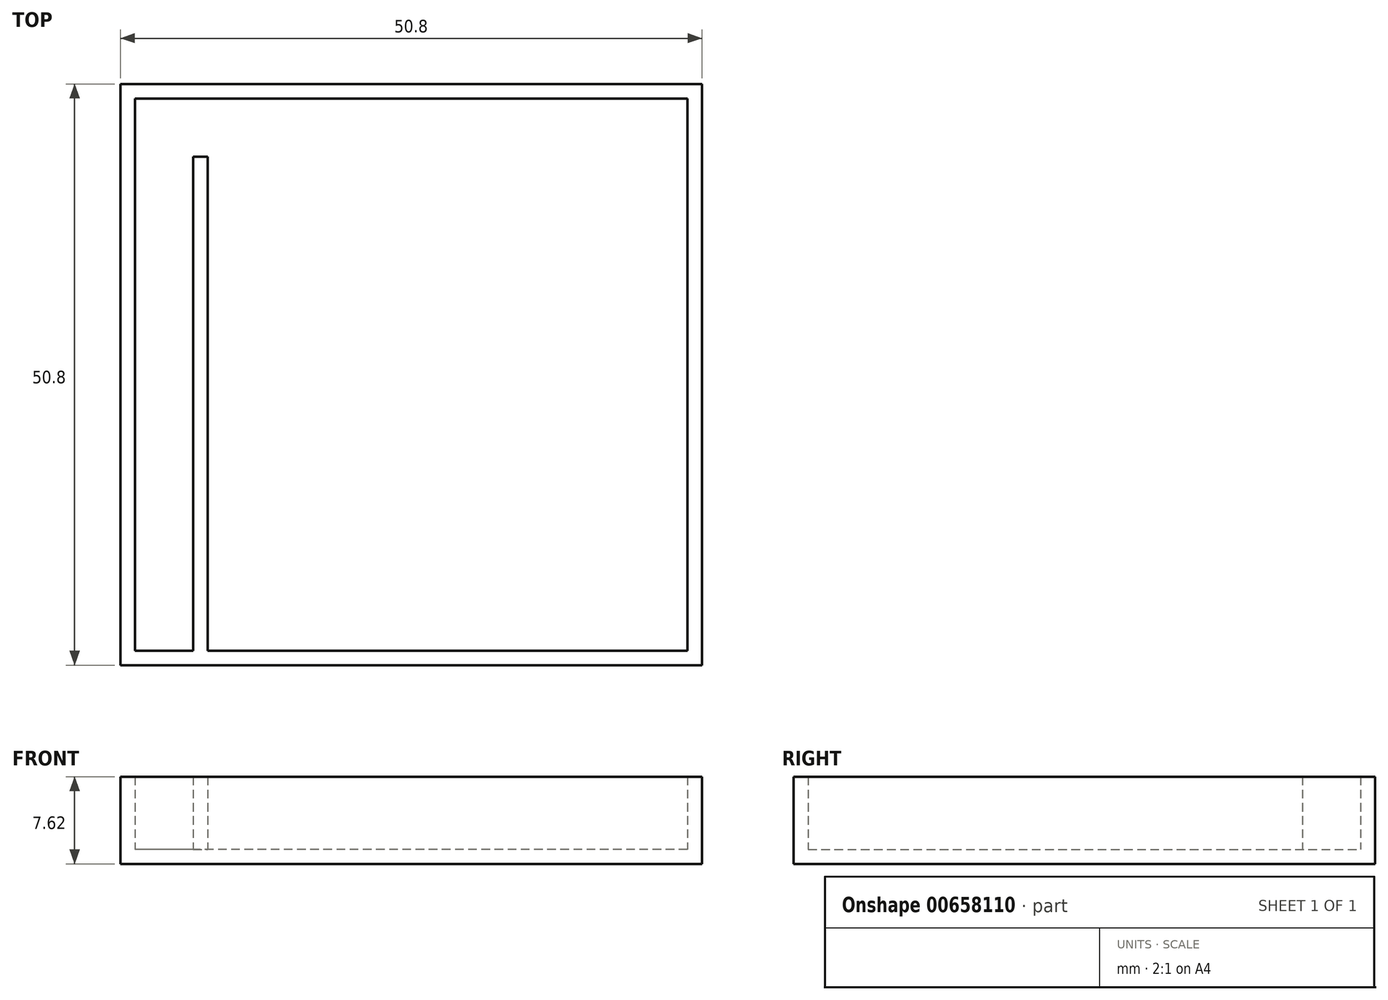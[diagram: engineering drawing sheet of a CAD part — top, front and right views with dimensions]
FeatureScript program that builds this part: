
annotation { "Feature Type Name" : "Feature", "Feature Type Description" : "" }
export const myFeature = defineFeature(function(context is Context, id is Id, definition is map)
    precondition{}
    {
        {
            var Q0;
            Q0=qCreatedBy(makeId("Top.planeOp"),FACE);
            var sketch = newSketch(context, id + "F0", { "sketchPlane" : qUnion([Q0])});
            skLineSegment(sketch, "E0.bottom", {"start": v(0, 0) * mm, "end": v(-50.8, 0) * mm});
            skLineSegment(sketch, "E0.top", {"start": v(0, 50.8) * mm, "end": v(-50.8, 50.8) * mm});
            skLineSegment(sketch, "E0.left", {"start": v(0, 0) * mm, "end": v(0, 50.8) * mm});
            skLineSegment(sketch, "E0.right", {"start": v(-50.8, 0) * mm, "end": v(-50.8, 50.8) * mm});
            skSolve(sketch);
        }
        {
            var Q0;
            Q0 = qSketchRegion(id + "F0", true);
            extrude(context, id + "F1", {"entities" : qUnion([Q0]), "depth" : 7.62 * mm, "offsetDistance" : 25.4 * mm});
        }
        {
            var Q0;
            Q0=makeQuery(id+"F1.opExtrude","CAP_FACE",FACE,{"disambiguationData":[OSD([sQuery(id+"F0.wireOp",EDGE,"E0.bottom"),sQuery(id+"F0.wireOp",EDGE,"E0.top"),sQuery(id+"F0.wireOp",EDGE,"E0.left"),sQuery(id+"F0.wireOp",EDGE,"E0.right")])],"isStart":false});
            shell(context, id + "F2", {"entities" : qUnion([Q0]), "thickness" : 1.27 * mm});
        }
        {
            var Q0;
            Q0=makeQuery(id+"F2.opShell","OFFSET_FACE",FACE,{"disambiguationData":[OSD([sQuery(id+"F0.wireOp",EDGE,"E0.bottom"),sQuery(id+"F0.wireOp",EDGE,"E0.top"),sQuery(id+"F0.wireOp",EDGE,"E0.left"),sQuery(id+"F0.wireOp",EDGE,"E0.right")])]});
            var sketch = newSketch(context, id + "F3", { "sketchPlane" : qUnion([Q0])});
            skLineSegment(sketch, "E1", {"start": v(-49.53, 1.27) * mm, "end": v(-44.45, 1.27) * mm});
            skLineSegment(sketch, "E2.bottom", {"start": v(-44.45, 1.27) * mm, "end": v(-43.18, 1.27) * mm});
            skLineSegment(sketch, "E2.top", {"start": v(-44.45, 44.45) * mm, "end": v(-43.18, 44.45) * mm});
            skLineSegment(sketch, "E2.left", {"start": v(-44.45, 1.27) * mm, "end": v(-44.45, 44.45) * mm});
            skLineSegment(sketch, "E2.right", {"start": v(-43.18, 1.27) * mm, "end": v(-43.18, 44.45) * mm});
            skSolve(sketch);
        }
        {
            var Q0;
            Q0 = qSketchRegion(id + "F3", true);
            extrude(context, id + "F4", {"entities" : qUnion([Q0]), "operationType" : NewBodyOperationType.ADD, "depth" : 6.35 * mm, "offsetDistance" : 25.4 * mm});
        }
    });
